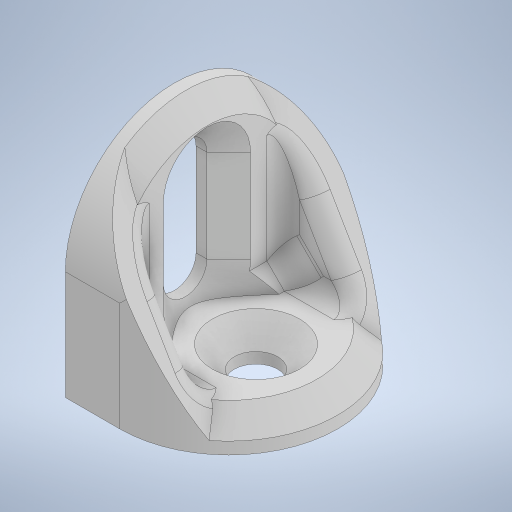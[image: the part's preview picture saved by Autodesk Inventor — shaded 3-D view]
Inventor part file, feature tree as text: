
AUTODESK INVENTOR PART (.ipt)
format: ipt  version: 2024.1 (Build 281209000, 209)  size: 463,872 bytes
history: native  units: in
note: dims shown in document units (in); Inventor stores cm internally (conversion verified against a paired STEP export)
features: extrude x5, sketch x5, fillet x3, chamfer x3, plane x2, other x1, mirror x1, projected_geometry x1
ambient origin geometry x8: Origin, YZ Plane, XZ Plane, XY Plane, X Axis, Y Axis, Z Axis, Center Point
bodies: Body1 (feature_tree)
feature tree (21):
  other  "bracket"
  extrude  "Extrusion1"  Depth=0.5906in
  extrude  "Extrusion2"  Depth=0.1181in
  extrude  "Extrusion3"  Depth=0.1575in
  extrude  "Extrusion4"  Depth=0.3937in
  plane  "Work Plane1"
  extrude  "Extrusion5"  Depth=0.2953in
  plane  "Work Plane3"
  mirror  "Mirror3"
  fillet  "Fillet1"  Radius=1.063in
  fillet  "Fillet2"  Radius=0.1575in
  fillet  "Fillet3"  Radius=0.7874in
  chamfer  "Chamfer2"  Distance=0.3937in
  chamfer  "Chamfer3"  Distance=0.7874in
  chamfer  "Chamfer4"  Distance=0.3937in
  sketch  "Sketch1"  dims[d0=0.7874in d1=0.5906in]
  sketch  "Sketch2"  dims[d2=0.1181in d3=0.0in d4=0.1181in]
  sketch  "Sketch3"  dims[d5=0.6693in d6=0.0in d7=0.1575in]
  sketch  "Sketch4"  dims[d8=0.7874in d9=0.3937in]
  sketch  "Sketch7"  dims[d12=0.5906in d13=0.2953in d14=1.063in d15=0.0in d16=0.1575in d17=0.7874in d18=0.3937in d19=0.7874in d20=0.3937in d21=1.063in d22=0.0in d27=0.0in d28=0.1969in d29=0.1969in d30=0.1181in d31=0.0in d32=0.3937in d36=0.0669in d37=0.0591in d38=0.0748in d39=0.0787in d40=45.0deg d56=0.2165in d57=0.2362in d58=0.0787in d59=0.0787in d60=45.0deg d61=0.063in d62=0.0787in d63=45.0deg]
  projected_geometry  "Projected Loop1"
